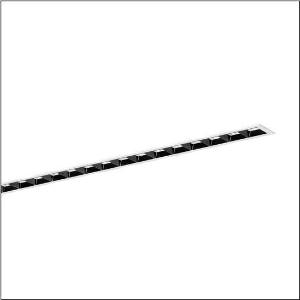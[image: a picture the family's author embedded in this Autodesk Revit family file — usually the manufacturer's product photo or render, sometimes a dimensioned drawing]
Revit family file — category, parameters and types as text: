
# Revit family: silica_r__21_51mx12tat4w_4f36
name_source: partatom
category: Lighting Fixtures
units: mm (PartAtom-declared; Revit-internal decimal feet)

## family parameters
Cut with Voids When Loaded = No
Host = Face
Light Source = No
Part Type = Normal
Room Calculation Point = No
Round Connector Dimension = Use Diameter
Shared = No

## types (1)
- --- (1 x LED, 3720 lm, 32.1 W, 6500K)
    Apparent Load = 32 VA
    CIE Flux Codes = 84 100 100 100 100
    Color Rendering = 80
    Color Temperature = 6500K
    Default Elevation = 1800 mm
    Description = Silica® 21, office luminaire, primary light control with darklight reflector, of PMMA, black, CAT 2 (L<= 3000cd/m²), light emission: direct distribution, primary light characteristic: symmetric, installation type: recessed, LED, rated luminous flux: 3.720lm, luminous efficacy: 110lm/W, light colour: 8tw, colour temperature: 2700..6500K, with terminal, 3+2-pole, max. 2.5mm², mains connection: 220..240V, AC, 50/60Hz, rated input power: 33.8W, luminaire housing, of aluminium, traffic white (RAL 9016), length: 1.228mm, width: 79mm, height: 53mm, protection rating (complete): IP20, insulation class (complete): insulation class I (protective earthing), certification: CE, permissible operating ambient temperature: 0..+35°C, standard: EN 50419, packaging unit: 1 piece
    Height = 0 mm  [stored 0 ft]
    Lamp = 1 x LED
    Lamp Light Flux = 3720 lm
    Lamp Power = 32.1 W
    Lamp count = 1
    Length = 1227 mm
    Luminous efficacy = 116 lm/W
    Manufacturer = Siteco
    ModVariant = No
    Model = 51MX12TAT4W
    Mounting Place = Ceiling
    Mounting Type = Recessed
    Number of Poles = 1
    OnlyDefault = Yes
    Power Factor = 1
    Product Name = Silica® 21
    Product group = office luminaire | ceiling recessed
    ProductGroupID = 401
    Protection Class = Protection class I
    Protection Degree = IP 20
    RLX_Detail_Level = 1
    RLX_Emergency_Light_Flux = 0 lm
    RLX_Emergency_Type = 0
    RLX_Emergency_Type_DB = No
    RlxData = <blob elided: 36661 chars, md5=b398ade0>
    Socket = socket
    Standby Power = 0 W
    System Light Flux = 3720 lm
    System Power = 32 W
    Type Comments = individual setting
    Type Image = l_1313610.jpg
    URL = http://relux.com
    VarID = @adj_089547
    Voltage = 0 V
    Weight = 0.00 kg
    Width = 79 mm

note: [stored X ft] marks values corroborated as IEEE doubles in the binary element streams (Revit-internal decimal feet)

## geometry (parser evidence)
native form markers: Blend x4, Sweep x11
no freeform markers — native parametric forms only
